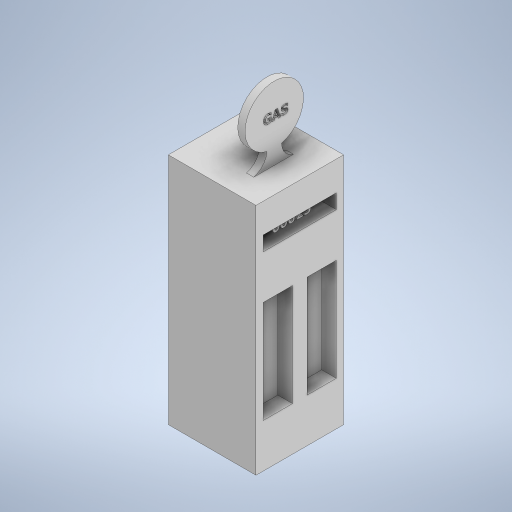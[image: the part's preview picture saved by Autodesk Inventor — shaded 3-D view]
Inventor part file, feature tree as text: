
AUTODESK INVENTOR PART (.ipt)
format: ipt  version: 2023 (Build 270158000, 158)  size: 499,712 bytes
history: native  units: mm
features: extrude x6, sketch x6
ambient origin geometry x8: Origin, YZ Plane, XZ Plane, XY Plane, X Axis, Y Axis, Z Axis, Center Point
bodies: Solid1 (feature_tree)
feature tree (12):
  extrude  "Extrusion1"  Depth=10.0mm
  extrude  "Extrusion2"  Depth=30.0mm
  extrude  "Extrusion3"  Depth=10.0mm
  extrude  "Extrusion4"  Depth=80.0mm TaperAngle=0.0deg
  extrude  "Extrusion5"  Depth=15.0mm
  extrude  "Extrusion6"  Depth=15.0mm
  sketch  "Sketch1"  dims[d0=10.0mm d1=10.0mm]
  sketch  "Sketch2"  dims[d2=5.0mm d3=0.0mm d4=30.0mm]
  sketch  "Sketch3"  dims[d5=30.0mm d6=10.0mm]
  sketch  "Sketch4"  dims[d7=10.0mm d8=80.0mm d9=0.0mm]
  sketch  "Sketch5"  dims[d10=20.0mm d11=15.0mm]
  sketch  "Sketch6"  dims[d13=2.5mm d14=15.0mm d15=2.5mm d16=0.0mm d17=2.5mm d18=0.0mm d19=10.0mm d20=5.0mm d21=25.0mm d22=2.5mm d23=10.0mm d24=10.0mm d25=15.0mm d26=15.0mm d27=35.0mm d28=5.0mm d29=0.0mm d30=2.5mm d31=0.0mm]
